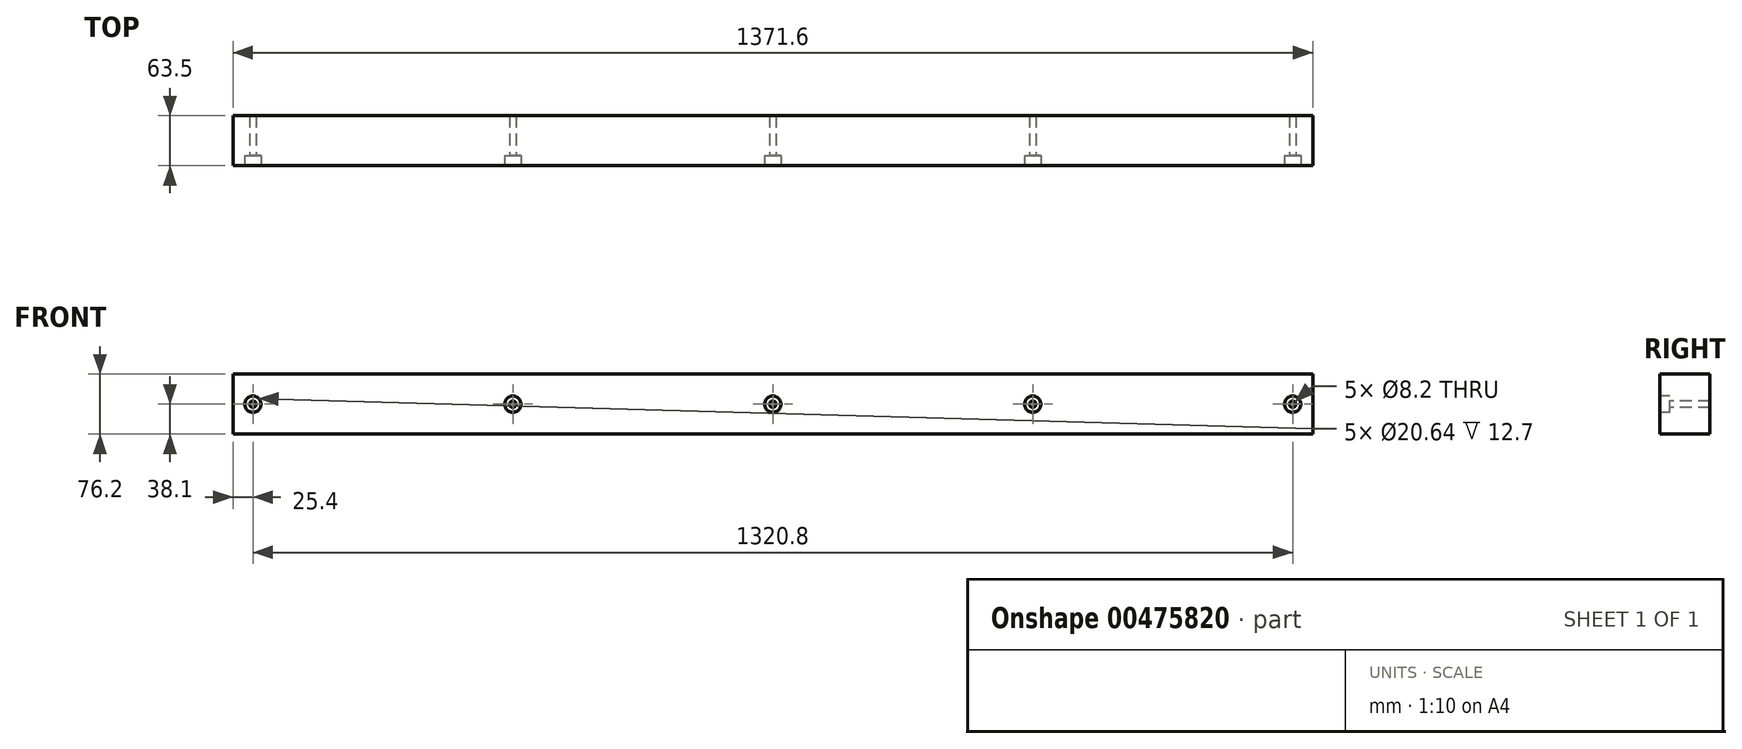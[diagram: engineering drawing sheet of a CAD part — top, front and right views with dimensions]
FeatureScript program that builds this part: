
annotation { "Feature Type Name" : "Feature", "Feature Type Description" : "" }
export const myFeature = defineFeature(function(context is Context, id is Id, definition is map)
    precondition{}
    {
        {
            var Q0;
            Q0=qCreatedBy(makeId("Front.planeOp"),FACE);
            var sketch = newSketch(context, id + "F0", { "sketchPlane" : qUnion([Q0])});
            skLineSegment(sketch, "E0.bottom", {"start": v(685.8, -38.1) * mm, "end": v(-685.8, -38.1) * mm});
            skLineSegment(sketch, "E0.top", {"start": v(685.8, 38.1) * mm, "end": v(-685.8, 38.1) * mm});
            skLineSegment(sketch, "E0.left", {"start": v(685.8, -38.1) * mm, "end": v(685.8, 38.1) * mm});
            skLineSegment(sketch, "E0.right", {"start": v(-685.8, -38.1) * mm, "end": v(-685.8, 38.1) * mm});
            skPoint(sketch, "E0.middle", {"position": v(0, 0) * mm});
            skLineSegment(sketch, "E1", {"start": v(-685.8, 0) * mm, "end": v(685.8, 0) * mm, "construction": true});
            skPoint(sketch, "E2", {"position": v(-660.4, 0) * mm});
            skPoint(sketch, "E3", {"position": v(660.4, 0) * mm});
            skPoint(sketch, "E4", {"position": v(330.2, 0) * mm});
            skPoint(sketch, "E5", {"position": v(-330.2, 0) * mm});
            skSolve(sketch);
        }
        {
            var Q0;
            Q0 = qSketchRegion(id + "F0", true);
            extrude(context, id + "F1", {"entities" : qUnion([Q0]), "oppositeDirection" : true, "depth" : 63.5 * mm});
        }
        {
            var Q0;
            Q0=sQuery(id+"F0.wireOp",VERTEX,"E2");
            var Q1;
            Q1=sQuery(id+"F0.wireOp",VERTEX,"E5");
            var Q2;
            Q2=sQuery(id+"F0.wireOp",VERTEX,"E0.middle");
            var Q3;
            Q3=sQuery(id+"F0.wireOp",VERTEX,"E4");
            var Q4;
            Q4=sQuery(id+"F0.wireOp",VERTEX,"E3");
            var Q5;
            Q5=makeQuery(id+"F1.opExtrude","SWEPT_BODY",BODY,{"disambiguationData":[OSD([sQuery(id+"F0.wireOp",EDGE,"E0.bottom"),sQuery(id+"F0.wireOp",EDGE,"E0.top"),sQuery(id+"F0.wireOp",EDGE,"E0.left"),sQuery(id+"F0.wireOp",EDGE,"E0.right")])]});
            hole(context, id + "F2", {"style" : HoleStyle.C_BORE, "endStyle" : HoleEndStyle.THROUGH, "holeDiameter" : 8.2 * mm, "cBoreDiameter" : 20.64 * mm, "cBoreDepth" : 12.7 * mm, "tappedDepth" : 12 * mm, "tapClearance" : 3, "startFromSketch" : true, "locations" : qUnion([Q0, Q1, Q2, Q3, Q4]), "scope" : qUnion([Q5])});
        }
    });
